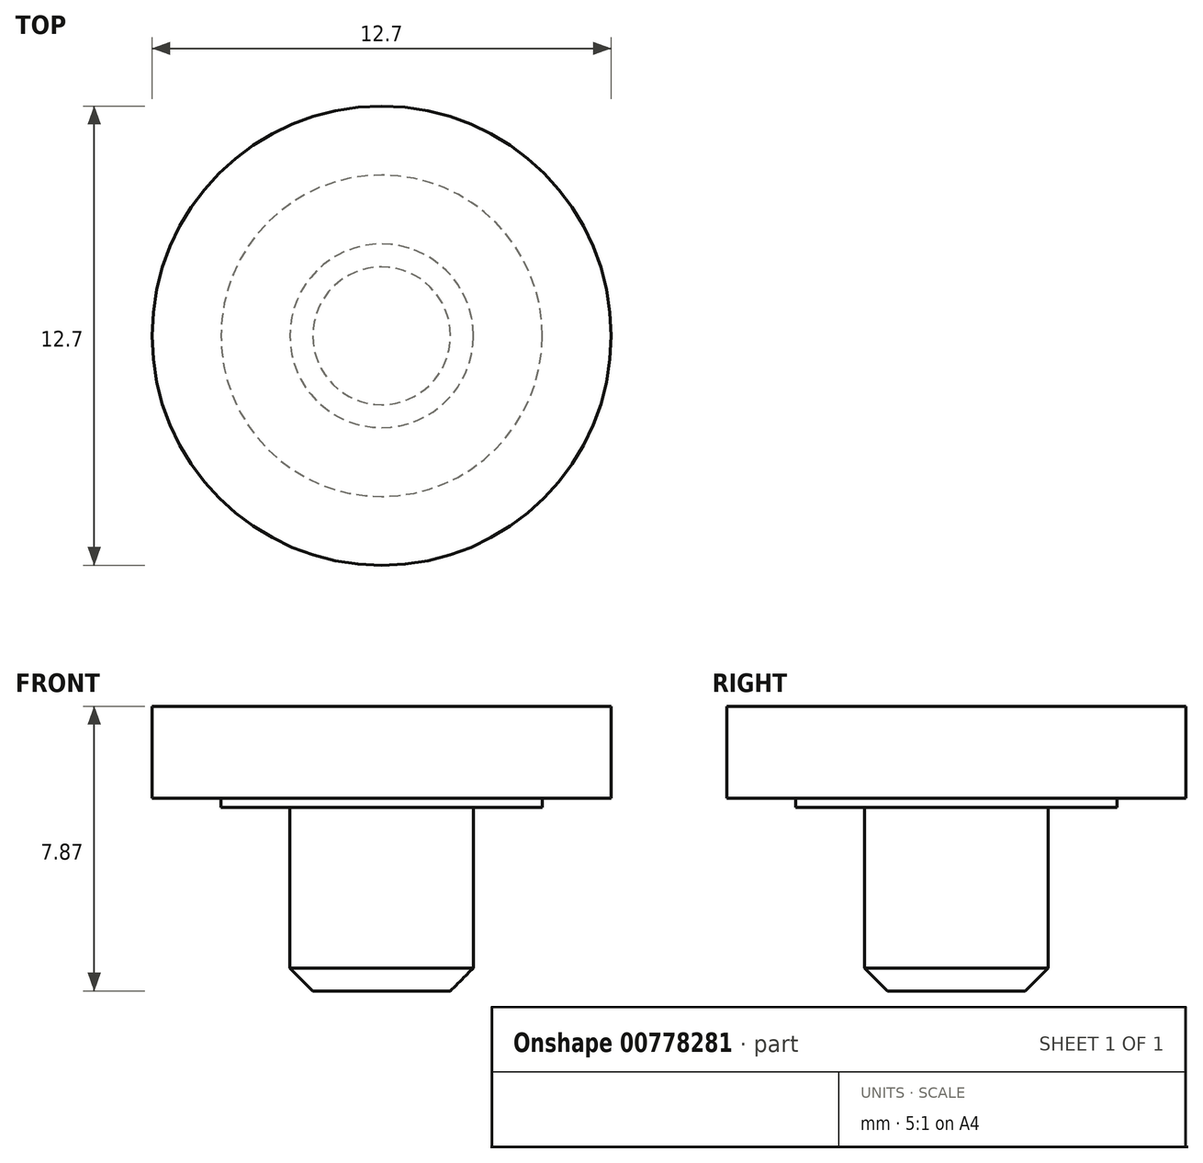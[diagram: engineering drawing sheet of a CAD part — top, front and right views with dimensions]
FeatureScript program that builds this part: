
annotation { "Feature Type Name" : "Feature", "Feature Type Description" : "" }
export const myFeature = defineFeature(function(context is Context, id is Id, definition is map)
    precondition{}
    {
        {
            var Q0;
            Q0=qCreatedBy(makeId("Top.planeOp"),FACE);
            var sketch = newSketch(context, id + "F0", { "sketchPlane" : qUnion([Q0])});
            skCircle(sketch, "E0", {"center": v(0, 0) * mm, "radius": 2.54 * mm});
            skSolve(sketch);
        }
        {
            var Q0;
            Q0=qSketchRegion(id+"F0",true);
            extrude(context, id + "F1", {"entities" : qUnion([Q0]), "depth" : 5.08 * mm, "offsetDistance" : 25.4 * mm});
        }
        {
            var Q0;
            Q0=makeQuery(id+"F1.opExtrude","CAP_FACE",FACE,{"disambiguationData":[OSD([sQuery(id+"F0.wireOp",EDGE,"E0")])],"isStart":false});
            var sketch = newSketch(context, id + "F2", { "sketchPlane" : qUnion([Q0])});
            skCircle(sketch, "E1", {"center": v(0, 0) * mm, "radius": 4.45 * mm});
            skSolve(sketch);
        }
        {
            var Q0;
            Q0=qSketchRegion(id+"F2",true);
            extrude(context, id + "F3", {"entities" : qUnion([Q0]), "operationType" : NewBodyOperationType.ADD, "depth" : 0.25 * mm, "offsetDistance" : 25.4 * mm});
        }
        {
            var Q0;
            Q0=makeQuery(id+"F3.opExtrude","CAP_FACE",FACE,{"disambiguationData":[OSD([sQuery(id+"F2.wireOp",EDGE,"E1")])],"isStart":false});
            var sketch = newSketch(context, id + "F4", { "sketchPlane" : qUnion([Q0])});
            skCircle(sketch, "E2", {"center": v(0, 0) * mm, "radius": 6.35 * mm});
            skSolve(sketch);
        }
        {
            var Q0;
            Q0=qSketchRegion(id+"F4",true);
            extrude(context, id + "F5", {"entities" : qUnion([Q0]), "operationType" : NewBodyOperationType.ADD, "depth" : 2.54 * mm, "offsetDistance" : 25.4 * mm});
        }
        {
            var Q0;
            Q0=makeQuery(id+"F1.opExtrude","CAP_EDGE",EDGE,{"disambiguationData":[OSD([sQuery(id+"F0.wireOp",EDGE,"E0")])],"isStart":true});
            chamfer(context, id + "F6", {"entities" : qUnion([Q0]), "width" : 0.64 * mm, "tangentPropagation" : true});
        }
    });
